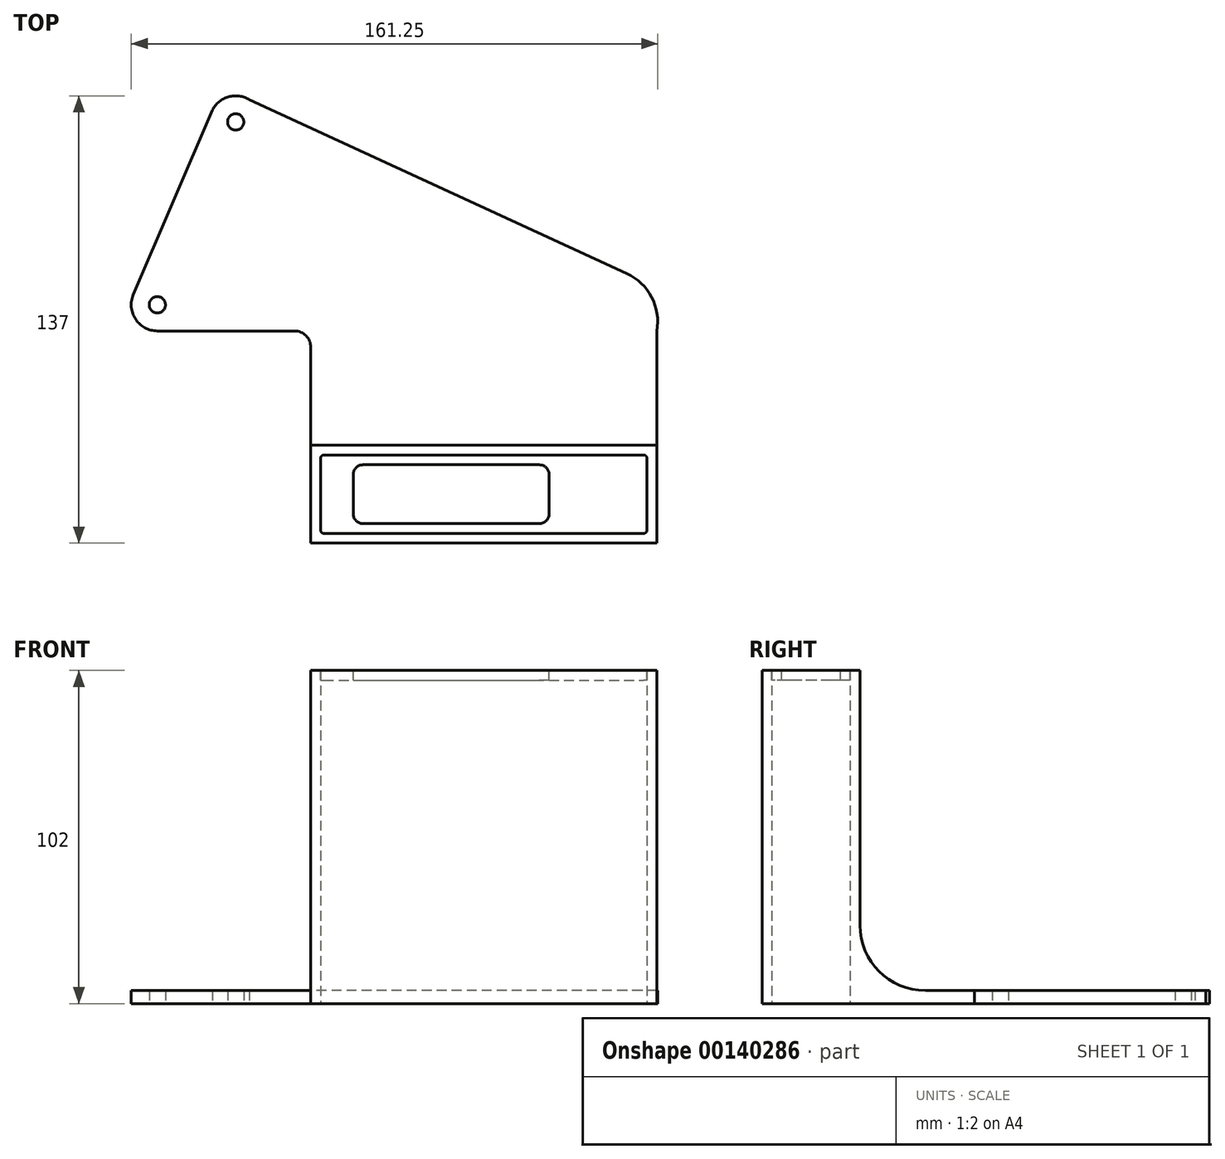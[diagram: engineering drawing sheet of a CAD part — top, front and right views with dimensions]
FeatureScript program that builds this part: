
annotation { "Feature Type Name" : "Feature", "Feature Type Description" : "" }
export const myFeature = defineFeature(function(context is Context, id is Id, definition is map)
    precondition{}
    {
        {
            var Q0;
            Q0=qCreatedBy(makeId("Top.planeOp"),FACE);
            var sketch = newSketch(context, id + "F0", { "sketchPlane" : qUnion([Q0])});
            skLineSegment(sketch, "E0", {"start": v(0, 0) * mm, "end": v(0, 56) * mm, "construction": true});
            skLineSegment(sketch, "E1", {"start": v(0, 56) * mm, "end": v(24, 56) * mm, "construction": true});
            skArc(sketch, "E2", {"start": v(28.13, 62.85) * mm, "mid": v(21.8, 63.7) * mm, "end": v(16.87, 59.63) * mm});
            skArc(sketch, "E3", {"start": v(-7.35, 3.15) * mm, "mid": v(-6.68, -4.4) * mm, "end": v(0, -8) * mm});
            skLineSegment(sketch, "E4", {"start": v(16.87, 59.63) * mm, "end": v(-7.35, 3.15) * mm});
            skLineSegment(sketch, "E5", {"start": v(0, -8) * mm, "end": v(42, -8) * mm});
            skLineSegment(sketch, "E6", {"start": v(143.79, 9.6) * mm, "end": v(28.13, 62.85) * mm});
            skLineSegment(sketch, "E7.top", {"start": v(153, -73) * mm, "end": v(47, -73) * mm});
            skLineSegment(sketch, "E7.left", {"start": v(153, -8) * mm, "end": v(153, -73) * mm});
            skLineSegment(sketch, "E7.right", {"start": v(47, -13) * mm, "end": v(47, -73) * mm});
            skPoint(sketch, "E8.newPointA", {"position": v(153, -8) * mm});
            skArc(sketch, "E8.filletArc", {"start": v(47, -13) * mm, "mid": v(45.54, -9.46) * mm, "end": v(42, -8) * mm});
            skArc(sketch, "E9", {"start": v(143.79, 9.6) * mm, "mid": v(151.4, 2.37) * mm, "end": v(153, -8) * mm});
            skCircle(sketch, "E10", {"center": v(0, 0) * mm, "radius": 2.5 * mm});
            skCircle(sketch, "E11", {"center": v(24, 56) * mm, "radius": 2.5 * mm});
            skSolve(sketch);
        }
        {
            var Q0;
            Q0 = qSketchRegion(id + "F0", true);
            extrude(context, id + "F1", {"entities" : qUnion([Q0]), "depth" : 4 * mm});
        }
        {
            var Q0;
            Q0=makeQuery(id+"F1.opExtrude","CAP_FACE",FACE,{"disambiguationData":[OSD([sQuery(id+"F0.wireOp",EDGE,"E2"),sQuery(id+"F0.wireOp",EDGE,"E3"),sQuery(id+"F0.wireOp",EDGE,"E4"),sQuery(id+"F0.wireOp",EDGE,"E5"),sQuery(id+"F0.wireOp",EDGE,"E6"),sQuery(id+"F0.wireOp",EDGE,"E7.top"),sQuery(id+"F0.wireOp",EDGE,"E7.left"),sQuery(id+"F0.wireOp",EDGE,"E7.right"),sQuery(id+"F0.wireOp",EDGE,"E8.filletArc"),sQuery(id+"F0.wireOp",EDGE,"E9"),sQuery(id+"F0.wireOp",EDGE,"E10"),sQuery(id+"F0.wireOp",EDGE,"E11")])],"isStart":true});
            var sketch = newSketch(context, id + "F2", { "sketchPlane" : qUnion([Q0])});
            skLineSegment(sketch, "E12", {"start": v(153, 73) * mm, "end": v(47, 73) * mm});
            skLineSegment(sketch, "E13", {"start": v(47, 73) * mm, "end": v(47, 43) * mm});
            skLineSegment(sketch, "E14", {"start": v(47, 43) * mm, "end": v(153, 43) * mm});
            skLineSegment(sketch, "E15", {"start": v(153, 43) * mm, "end": v(153, 73) * mm});
            skLineSegment(sketch, "E16.0", {"start": v(51, 46) * mm, "end": v(149, 46) * mm});
            skLineSegment(sketch, "E16.1", {"start": v(50, 69) * mm, "end": v(50, 47) * mm});
            skLineSegment(sketch, "E16.2", {"start": v(149, 70) * mm, "end": v(51, 70) * mm});
            skLineSegment(sketch, "E16.3", {"start": v(150, 47) * mm, "end": v(150, 69) * mm});
            skPoint(sketch, "E17.visualSharp", {"position": v(150, 46) * mm});
            skArc(sketch, "E17.filletArc", {"start": v(149, 46) * mm, "mid": v(149.7, 46.3) * mm, "end": v(150, 47) * mm});
            skPoint(sketch, "E18.visualSharp", {"position": v(150, 70) * mm});
            skArc(sketch, "E18.filletArc", {"start": v(150, 69) * mm, "mid": v(149.7, 69.7) * mm, "end": v(149, 70) * mm});
            skPoint(sketch, "E19.visualSharp", {"position": v(50, 70) * mm});
            skArc(sketch, "E19.filletArc", {"start": v(51, 70) * mm, "mid": v(50.3, 69.7) * mm, "end": v(50, 69) * mm});
            skPoint(sketch, "E20.visualSharp", {"position": v(50, 46) * mm});
            skArc(sketch, "E20.filletArc", {"start": v(50, 47) * mm, "mid": v(50.3, 46.3) * mm, "end": v(51, 46) * mm});
            skSolve(sketch);
        }
        {
            var Q0;
            Q0=makeQuery(id+"F2.imprint","IMPRINT",FACE,{"disambiguationData":[TD([[makeQuery(id+"F2.imprint","IMPRINT",EDGE,{"derivedFrom":sQuery(id+"F2.wireOp",EDGE,"E16.0")}),1.0]])]});
            extrude(context, id + "F3", {"entities" : qUnion([Q0]), "operationType" : NewBodyOperationType.REMOVE, "endBound" : BoundingType.THROUGH_ALL, "oppositeDirection" : true, "depth" : 25 * mm});
        }
        {
            var Q0;
            Q0 = qSketchRegion(id + "F2", true);
            extrude(context, id + "F4", {"entities" : qUnion([Q0]), "operationType" : NewBodyOperationType.ADD, "oppositeDirection" : true, "depth" : 77 * mm});
        }
        {
            var Q0;
            Q0=makeQuery(id+"F4.opExtrude","CAP_FACE",FACE,{"disambiguationData":[OSD([sQuery(id+"F2.wireOp",EDGE,"E12"),sQuery(id+"F2.wireOp",EDGE,"E13"),sQuery(id+"F2.wireOp",EDGE,"E14"),sQuery(id+"F2.wireOp",EDGE,"E15"),sQuery(id+"F2.wireOp",EDGE,"E16.0"),sQuery(id+"F2.wireOp",EDGE,"E16.1"),sQuery(id+"F2.wireOp",EDGE,"E16.2"),sQuery(id+"F2.wireOp",EDGE,"E16.3"),sQuery(id+"F2.wireOp",EDGE,"E17.filletArc"),sQuery(id+"F2.wireOp",EDGE,"E18.filletArc"),sQuery(id+"F2.wireOp",EDGE,"E19.filletArc"),sQuery(id+"F2.wireOp",EDGE,"E20.filletArc")])],"isStart":false});
            extrude(context, id + "F5", {"entities" : qUnion([Q0]), "operationType" : NewBodyOperationType.ADD, "depth" : 25 * mm});
        }
        {
            var Q0;
            Q0=makeQuery(id+"F5.opExtrude","CAP_FACE",FACE,{"disambiguationData":[OSD([sQuery(id+"F2.wireOp",EDGE,"E12"),sQuery(id+"F2.wireOp",EDGE,"E13"),sQuery(id+"F2.wireOp",EDGE,"E14"),sQuery(id+"F2.wireOp",EDGE,"E15"),sQuery(id+"F2.wireOp",EDGE,"E16.0"),sQuery(id+"F2.wireOp",EDGE,"E16.1"),sQuery(id+"F2.wireOp",EDGE,"E16.2"),sQuery(id+"F2.wireOp",EDGE,"E16.3"),sQuery(id+"F2.wireOp",EDGE,"E17.filletArc"),sQuery(id+"F2.wireOp",EDGE,"E18.filletArc"),sQuery(id+"F2.wireOp",EDGE,"E19.filletArc"),sQuery(id+"F2.wireOp",EDGE,"E20.filletArc")])],"isStart":false});
            var sketch = newSketch(context, id + "F6", { "sketchPlane" : qUnion([Q0])});
            skLineSegment(sketch, "E21.0", {"start": v(51, -46) * mm, "end": v(149, -46) * mm});
            skArc(sketch, "E21.1", {"start": v(50, -47) * mm, "mid": v(50.3, -46.3) * mm, "end": v(51, -46) * mm});
            skLineSegment(sketch, "E21.2", {"start": v(50, -69) * mm, "end": v(50, -47) * mm});
            skArc(sketch, "E21.3", {"start": v(51, -70) * mm, "mid": v(50.3, -69.7) * mm, "end": v(50, -69) * mm});
            skLineSegment(sketch, "E21.4", {"start": v(149, -70) * mm, "end": v(51, -70) * mm});
            skArc(sketch, "E21.5", {"start": v(149, -46) * mm, "mid": v(149.7, -46.3) * mm, "end": v(150, -47) * mm});
            skLineSegment(sketch, "E21.6", {"start": v(150, -47) * mm, "end": v(150, -69) * mm});
            skArc(sketch, "E21.7", {"start": v(150, -69) * mm, "mid": v(149.7, -69.7) * mm, "end": v(149, -70) * mm});
            skLineSegment(sketch, "E22", {"start": v(60, -52) * mm, "end": v(60, -64) * mm});
            skLineSegment(sketch, "E23", {"start": v(120, -64) * mm, "end": v(120, -52) * mm});
            skLineSegment(sketch, "E24", {"start": v(63, -67) * mm, "end": v(117, -67) * mm});
            skLineSegment(sketch, "E25", {"start": v(63, -49) * mm, "end": v(117, -49) * mm});
            skPoint(sketch, "E26.orphan", {"position": v(60, -46) * mm});
            skPoint(sketch, "E27.orphan", {"position": v(60, -70) * mm});
            skPoint(sketch, "E28.visualSharp", {"position": v(60, -49) * mm});
            skArc(sketch, "E28.filletArc", {"start": v(63, -49) * mm, "mid": v(60.88, -49.88) * mm, "end": v(60, -52) * mm});
            skPoint(sketch, "E29.visualSharp", {"position": v(60, -67) * mm});
            skArc(sketch, "E29.filletArc", {"start": v(60, -64) * mm, "mid": v(60.88, -66.12) * mm, "end": v(63, -67) * mm});
            skPoint(sketch, "E30.visualSharp", {"position": v(120, -67) * mm});
            skArc(sketch, "E30.filletArc", {"start": v(117, -67) * mm, "mid": v(119.12, -66.12) * mm, "end": v(120, -64) * mm});
            skPoint(sketch, "E31.visualSharp", {"position": v(120, -49) * mm});
            skArc(sketch, "E31.filletArc", {"start": v(120, -52) * mm, "mid": v(119.12, -49.88) * mm, "end": v(117, -49) * mm});
            skSolve(sketch);
        }
        {
            var Q0;
            Q0=makeQuery(id+"F6.imprint","IMPRINT",FACE,{"disambiguationData":[TD([[makeQuery(id+"F6.imprint","IMPRINT",EDGE,{"derivedFrom":sQuery(id+"F6.wireOp",EDGE,"E21.0")}),-1.0]])]});
            extrude(context, id + "F7", {"entities" : qUnion([Q0]), "oppositeDirection" : true, "depth" : 3 * mm});
        }
        {
            var Q0;
            Q0=makeQuery(id+"F4.boolean.opBoolean","INTERSECT",EDGE,{"derivedFrom":[makeQuery(id+"F1.opExtrude","CAP_FACE",FACE,{"disambiguationData":[OSD([sQuery(id+"F0.wireOp",EDGE,"E2"),sQuery(id+"F0.wireOp",EDGE,"E3"),sQuery(id+"F0.wireOp",EDGE,"E4"),sQuery(id+"F0.wireOp",EDGE,"E5"),sQuery(id+"F0.wireOp",EDGE,"E6"),sQuery(id+"F0.wireOp",EDGE,"E7.top"),sQuery(id+"F0.wireOp",EDGE,"E7.left"),sQuery(id+"F0.wireOp",EDGE,"E7.right"),sQuery(id+"F0.wireOp",EDGE,"E8.filletArc"),sQuery(id+"F0.wireOp",EDGE,"E9"),sQuery(id+"F0.wireOp",EDGE,"E10"),sQuery(id+"F0.wireOp",EDGE,"E11")])],"isStart":false}),makeQuery(id+"F4.opExtrude","SWEPT_FACE",FACE,{"disambiguationData":[OSD([sQuery(id+"F2.wireOp",EDGE,"E14")])]})]});
            fillet(context, id + "F8", {"entities" : qUnion([Q0]), "radius" : 20 * mm, "tangentPropagation" : true, "allowEdgeOverflow" : false});
        }
    });
